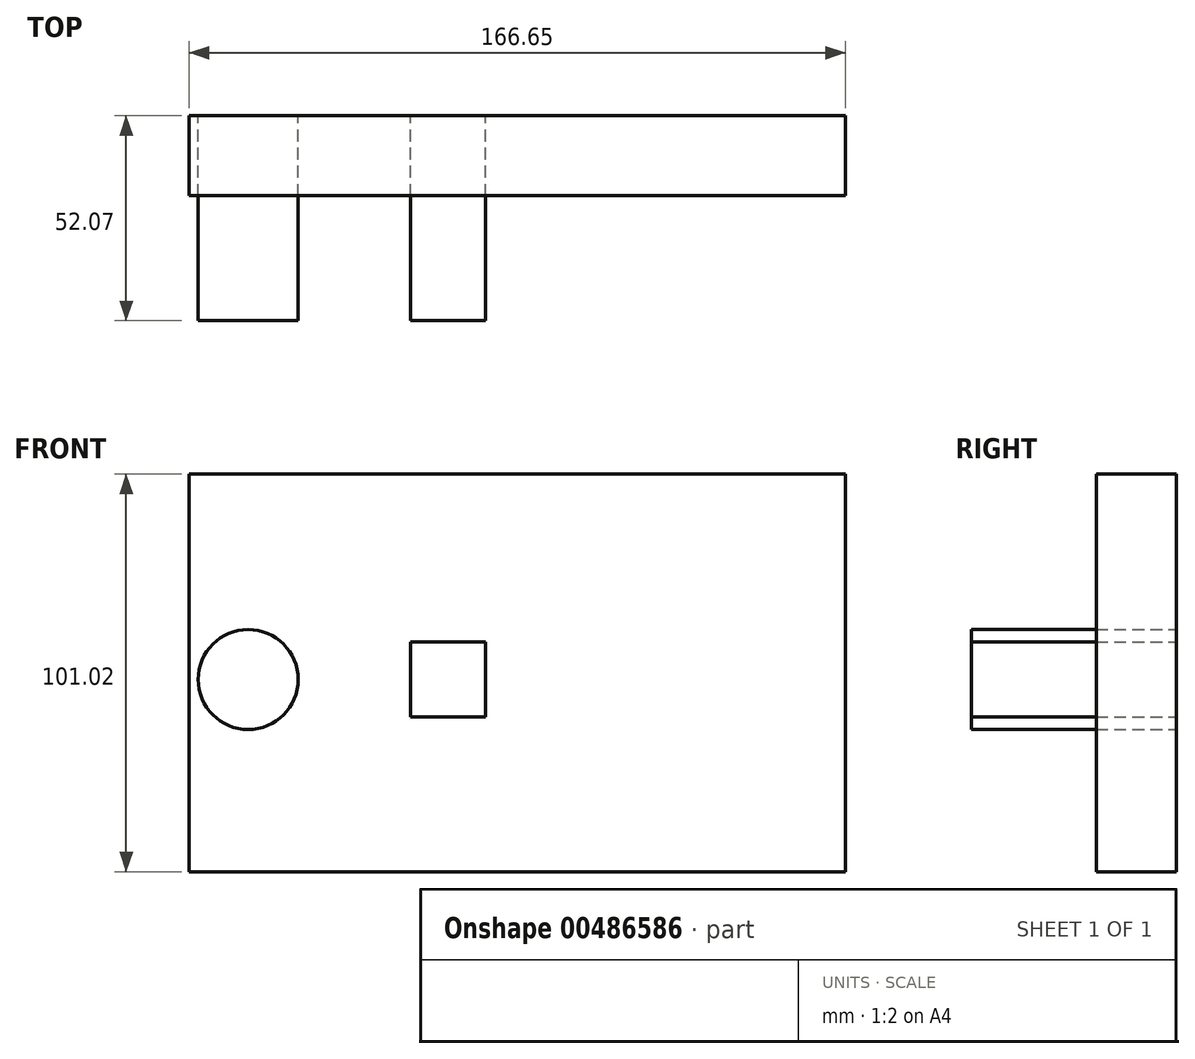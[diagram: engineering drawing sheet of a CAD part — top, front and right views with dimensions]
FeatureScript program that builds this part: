
annotation { "Feature Type Name" : "Feature", "Feature Type Description" : "" }
export const myFeature = defineFeature(function(context is Context, id is Id, definition is map)
    precondition{}
    {
        {
            var Q0;
            Q0=qCreatedBy(makeId("Front.planeOp"),FACE);
            var sketch = newSketch(context, id + "F0", { "sketchPlane" : qUnion([Q0])});
            skLineSegment(sketch, "E0", {"start": v(0, 0) * mm, "end": v(6.35, 0) * mm});
            skLineSegment(sketch, "E1", {"start": v(6.35, 0) * mm, "end": v(-6.35, -22) * mm});
            skLineSegment(sketch, "E2", {"start": v(-6.35, -22) * mm, "end": v(6.35, 0) * mm});
            skLineSegment(sketch, "E3", {"start": v(6.35, 0) * mm, "end": v(19.05, -22) * mm});
            skLineSegment(sketch, "E4", {"start": v(19.05, -22) * mm, "end": v(-6.35, -22) * mm});
            skLineSegment(sketch, "E5", {"start": v(0, 0) * mm, "end": v(-31.75, 0) * mm});
            skLineSegment(sketch, "E6.bottom", {"start": v(-22.23, -9.52) * mm, "end": v(-41.28, -9.52) * mm});
            skLineSegment(sketch, "E6.top", {"start": v(-22.23, 9.53) * mm, "end": v(-41.27, 9.53) * mm});
            skLineSegment(sketch, "E6.left", {"start": v(-22.23, -9.52) * mm, "end": v(-22.23, 9.53) * mm});
            skLineSegment(sketch, "E6.right", {"start": v(-41.27, -9.52) * mm, "end": v(-41.27, 9.53) * mm});
            skPoint(sketch, "E6.middle", {"position": v(-31.75, 0) * mm});
            skLineSegment(sketch, "E7", {"start": v(-31.75, 0) * mm, "end": v(-82.55, 0) * mm});
            skCircle(sketch, "E8", {"center": v(-82.55, 0) * mm, "radius": 12.7 * mm});
            skSolve(sketch);
        }
        {
            var Q0;
            Q0=qCreatedBy(makeId("Front.planeOp"),FACE);
            var sketch = newSketch(context, id + "F1", { "sketchPlane" : qUnion([Q0])});
            skLineSegment(sketch, "E9.bottom", {"start": v(-97.52, 52.17) * mm, "end": v(69.13, 52.17) * mm});
            skLineSegment(sketch, "E9.top", {"start": v(-97.52, -48.85) * mm, "end": v(69.13, -48.85) * mm});
            skLineSegment(sketch, "E9.left", {"start": v(-97.52, 52.17) * mm, "end": v(-97.52, -48.85) * mm});
            skLineSegment(sketch, "E9.right", {"start": v(69.13, 52.17) * mm, "end": v(69.13, -48.85) * mm});
            skSolve(sketch);
        }
        {
            var Q0;
            Q0 = qSketchRegion(id + "F1", true);
            extrude(context, id + "F2", {"entities" : qUnion([Q0]), "depth" : 20.32 * mm});
        }
        {
            var Q0;
            Q0=makeQuery(id+"F0.imprint","IMPRINT",FACE,{"disambiguationData":[TD([[makeQuery(id+"F0.imprint","IMPRINT",EDGE,{"derivedFrom":sQuery(id+"F0.wireOp",EDGE,"E8")}),1.0]])]});
            var Q1;
            {var subQ1=sQuery(id+"F0.wireOp",EDGE,"E6.bottom");Q1=makeQuery(id+"F0.imprint","IMPRINT",FACE,{"disambiguationData":[TD([[makeQuery(id+"F0.imprint","IMPRINT",EDGE,{"derivedFrom":subQ1}),-1.0]])]});}
            var Q2;
            {var subQ1=sQuery(id+"F0.wireOp",EDGE,"E6.top");Q2=makeQuery(id+"F0.imprint","IMPRINT",FACE,{"disambiguationData":[TD([[makeQuery(id+"F0.imprint","IMPRINT",EDGE,{"derivedFrom":subQ1}),1.0]])]});}
            extrude(context, id + "F3", {"entities" : qUnion([Q0, Q1, Q2]), "depth" : 52.07 * mm});
        }
    });
